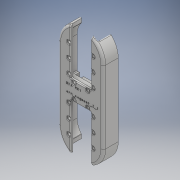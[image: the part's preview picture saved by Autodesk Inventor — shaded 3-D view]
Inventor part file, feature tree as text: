
AUTODESK INVENTOR PART (.ipt)
format: ipt  version: 2018 (Build 220112000, 112)  size: 3,310,080 bytes
history: native  units: mm
features: sketch x6, extrude x5, fillet x4, emboss x1, hole x1, projected_geometry x1
ambient origin geometry x8: Origin, YZ Plane, XZ Plane, XY Plane, X Axis, Y Axis, Z Axis, Center Point
bodies: Solid1 (feature_tree)
feature tree (18):
  extrude  "Extrusion1"  Depth=0.5mm
  extrude  "Extrusion2"  Depth=90.0mm
  sketch  "Sketch3"  dims[d4=56.0mm d5=28.0mm]
  extrude  "Extrusion3"  Depth=28.0mm
  extrude  "Extrusion4"  Depth=0.4mm
  fillet  "Fillet1"  Radius=0.4mm
  emboss  "Emboss1"
  fillet  "Fillet2"  Radius=0.4mm
  extrude  "Extrusion5"  Depth=0.4mm
  fillet  "Fillet3"  Radius=0.4mm
  hole  "Hole1"  [1 undecoded]
  fillet  "Fillet4"  Radius=3.0mm
  sketch  "Sketch1"  dims[d0=0.5mm d1=0.5mm]
  sketch  "Sketch2"  dims[d2=0.5mm d3=90.0mm]
  projected_geometry  "Projected Loop1"
  sketch  "Sketch4"  dims[d6=0.4mm d7=0.4mm d8=0.4mm d9=0.4mm]
  sketch  "Sketch5"  dims[d10=0.4mm d11=0.4mm d12=0.4mm]
  sketch  "Sketch6"  dims[d13=0.4mm d14=28.0mm d15=3.0mm d16=0.0mm d17=56.0mm d20=5.0mm d21=15.5mm d22=0.0mm d23=40.0mm d24=5.0mm d25=28.0mm d26=0.5mm d27=0.5mm d28=4.5mm d29=5.0mm d30=0.0mm d31=4.5mm d32=0.0mm d34=6.0mm d35=3.0mm d36=0.5mm d37=0.0mm d38=1.0mm d39=6.0mm d40=15.0mm d41=10.0mm d42=0.0mm d43=1.0mm d44=5.0mm d45=6.0mm d46=4.0mm d47=2.0mm d48=90.0deg d49=1.0mm d50=0.0mm d51=0.5mm]
note: 1 required parameter value undecoded (feature->parameter linkage not recoverable at this tier; creation-order binding heuristic only, values carry confidence <= 0.55)
